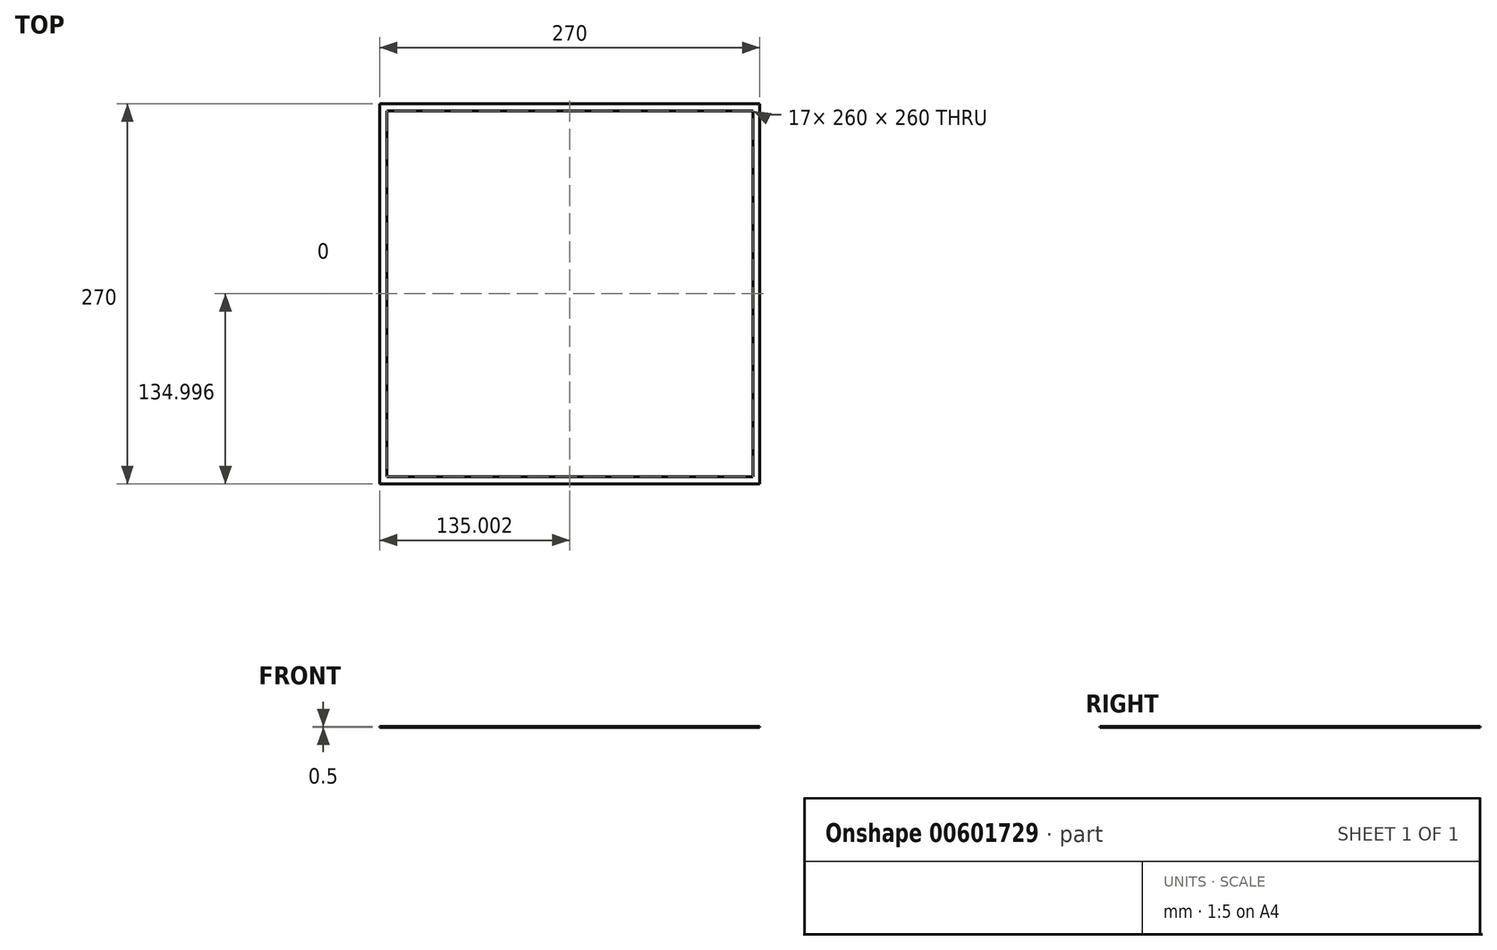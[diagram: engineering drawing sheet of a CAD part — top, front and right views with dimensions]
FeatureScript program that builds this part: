
annotation { "Feature Type Name" : "Feature", "Feature Type Description" : "" }
export const myFeature = defineFeature(function(context is Context, id is Id, definition is map)
    precondition{}
    {
        {
            var Q0;
            Q0=qCreatedBy(makeId("Top.planeOp"),FACE);
            var sketch = newSketch(context, id + "F0", { "sketchPlane" : qUnion([Q0])});
            skLineSegment(sketch, "E0.bottom", {"start": v(-212.92, 220.66) * mm, "end": v(57.08, 220.66) * mm});
            skLineSegment(sketch, "E0.top", {"start": v(-212.92, -49.34) * mm, "end": v(57.08, -49.34) * mm});
            skLineSegment(sketch, "E0.left", {"start": v(-212.92, 220.66) * mm, "end": v(-212.92, -49.34) * mm});
            skLineSegment(sketch, "E0.right", {"start": v(57.08, 220.66) * mm, "end": v(57.08, -49.34) * mm});
            skLineSegment(sketch, "E1.0", {"start": v(-207.92, 215.66) * mm, "end": v(52.08, 215.66) * mm});
            skLineSegment(sketch, "E1.1", {"start": v(-207.92, 215.66) * mm, "end": v(-207.92, -44.34) * mm});
            skLineSegment(sketch, "E1.2", {"start": v(-207.92, -44.34) * mm, "end": v(52.08, -44.34) * mm});
            skLineSegment(sketch, "E1.3", {"start": v(52.08, 215.66) * mm, "end": v(52.08, -44.34) * mm});
            skSolve(sketch);
        }
        {
            var Q0;
            Q0=makeQuery(id+"F0.imprint","IMPRINT",FACE,{"disambiguationData":[TD([[makeQuery(id+"F0.imprint","IMPRINT",EDGE,{"derivedFrom":sQuery(id+"F0.wireOp",EDGE,"E0.bottom")}),-1.0]])]});
            extrude(context, id + "F1", {"entities" : qUnion([Q0]), "depth" : .5 * mm, "offsetDistance" : 25 * mm});
        }
    });
